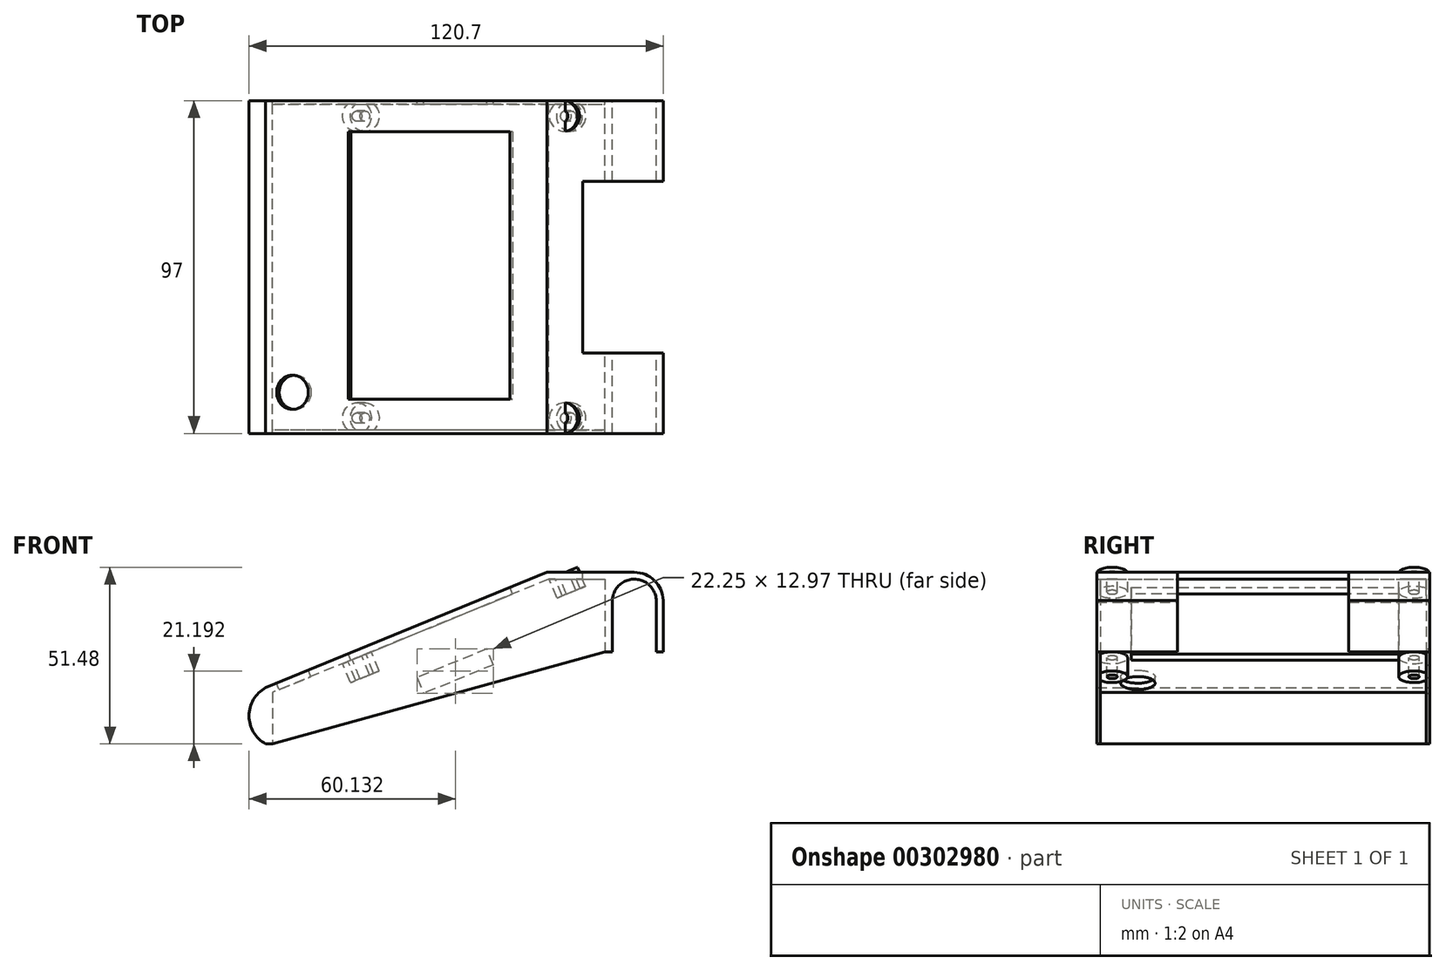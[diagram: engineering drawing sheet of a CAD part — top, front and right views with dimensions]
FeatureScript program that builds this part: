
annotation { "Feature Type Name" : "Feature", "Feature Type Description" : "" }
export const myFeature = defineFeature(function(context is Context, id is Id, definition is map)
    precondition{}
    {
        {
            var Q0;
            Q0=qCreatedBy(makeId("Front.planeOp"),FACE);
            var sketch = newSketch(context, id + "F0", { "sketchPlane" : qUnion([Q0])});
            skLineSegment(sketch, "E0", {"start": v(0, 0) * mm, "end": v(0, 33) * mm, "construction": true});
            skLineSegment(sketch, "E1", {"start": v(0, 33) * mm, "end": v(-80.5, 0) * mm});
            skLineSegment(sketch, "E2", {"start": v(-80.5, 0) * mm, "end": v(-80.5, -15) * mm});
            skLineSegment(sketch, "E3", {"start": v(-80.5, 0) * mm, "end": v(-74.8, -13.88) * mm, "construction": true});
            skLineSegment(sketch, "E4", {"start": v(0, 33) * mm, "end": v(16.42, 33) * mm});
            skLineSegment(sketch, "E5", {"start": v(25, 33) * mm, "end": v(25, 26.6) * mm, "construction": true});
            skArc(sketch, "E6", {"start": v(31.4, 26.3) * mm, "mid": v(25.07, 33) * mm, "end": v(18.6, 26.46) * mm});
            skLineSegment(sketch, "E7.0", {"start": v(-0.4, 35) * mm, "end": v(25.1, 35) * mm});
            skLineSegment(sketch, "E7.1", {"start": v(-0.4, 35) * mm, "end": v(-82.5, 1.34) * mm});
            skLineSegment(sketch, "E7.2", {"start": v(-82.5, 1.34) * mm, "end": v(-82.5, -15) * mm});
            skArc(sketch, "E8.0", {"start": v(33.4, 26.37) * mm, "mid": v(31.02, 32.46) * mm, "end": v(25, 35) * mm});
            skLineSegment(sketch, "E9", {"start": v(0, 33) * mm, "end": v(5.69, 19.12) * mm, "construction": true});
            skLineSegment(sketch, "E10", {"start": v(-82.5, -15) * mm, "end": v(-80.5, -15) * mm});
            skLineSegment(sketch, "E11", {"start": v(33.4, 26.83) * mm, "end": v(33.4, 11.83) * mm});
            skLineSegment(sketch, "E12", {"start": v(31.4, 26.9) * mm, "end": v(31.4, 11.83) * mm});
            skLineSegment(sketch, "E13", {"start": v(31.4, 11.83) * mm, "end": v(33.4, 11.83) * mm});
            skLineSegment(sketch, "E14", {"start": v(16.6, 26.37) * mm, "end": v(16.42, 33) * mm, "construction": true});
            skLineSegment(sketch, "E15", {"start": v(16.42, 33) * mm, "end": v(16.42, 11.83) * mm});
            skLineSegment(sketch, "E16", {"start": v(18.6, 26.46) * mm, "end": v(18.6, 11.83) * mm});
            skLineSegment(sketch, "E17", {"start": v(16.42, 11.83) * mm, "end": v(18.6, 11.83) * mm});
            skSolve(sketch);
        }
        {
            var Q0;
            Q0=makeQuery(id+"F0.imprint","IMPRINT",FACE,{"disambiguationData":[TD([[makeQuery(id+"F0.imprint","IMPRINT",EDGE,{"derivedFrom":sQuery(id+"F0.wireOp",EDGE,"E1")}),-1.0]])]});
            extrude(context, id + "F1", {"entities" : qUnion([Q0]), "endBound" : BoundingType.SYMMETRIC, "depth" : 97 * mm, "offsetDistance" : 25 * mm});
        }
        {
            var Q0;
            Q0=makeQuery(id+"F1.opExtrude","SWEPT_FACE",FACE,{"disambiguationData":[OSD([sQuery(id+"F0.wireOp",EDGE,"E1")])]});
            var sketch = newSketch(context, id + "F2", { "sketchPlane" : qUnion([Q0])});
            skLineSegment(sketch, "E18", {"start": v(17.18, 48.5) * mm, "end": v(17.18, 44) * mm, "construction": true});
            skCircle(sketch, "E19", {"center": v(17.18, 44) * mm, "radius": 1.5 * mm});
            skCircle(sketch, "E20", {"center": v(17.18, 44) * mm, "radius": 4.5 * mm});
            skLineSegment(sketch, "E21", {"start": v(17.18, 44) * mm, "end": v(-47.82, 44) * mm, "construction": true});
            skCircle(sketch, "E22", {"center": v(-47.82, 44) * mm, "radius": 1.5 * mm});
            skCircle(sketch, "E23", {"center": v(-47.82, 44) * mm, "radius": 4.5 * mm});
            skLineSegment(sketch, "E24", {"start": v(17.18, 44) * mm, "end": v(17.18, -44) * mm, "construction": true});
            skCircle(sketch, "E25", {"center": v(17.18, -44) * mm, "radius": 1.5 * mm});
            skCircle(sketch, "E26", {"center": v(17.18, -44) * mm, "radius": 4.5 * mm});
            skLineSegment(sketch, "E27", {"start": v(17.18, -44) * mm, "end": v(-47.82, -44) * mm, "construction": true});
            skCircle(sketch, "E28", {"center": v(-47.82, -44) * mm, "radius": 1.5 * mm});
            skCircle(sketch, "E29", {"center": v(-47.82, -44) * mm, "radius": 4.5 * mm});
            skSolve(sketch);
        }
        {
            var Q0;
            Q0=makeQuery(id+"F2.imprint","IMPRINT",FACE,{"disambiguationData":[TD([[makeQuery(id+"F2.imprint","IMPRINT",EDGE,{"derivedFrom":sQuery(id+"F2.wireOp",EDGE,"E19")}),-1.0]])]});
            var Q1;
            Q1=makeQuery(id+"F2.imprint","IMPRINT",FACE,{"disambiguationData":[TD([[makeQuery(id+"F2.imprint","IMPRINT",EDGE,{"derivedFrom":sQuery(id+"F2.wireOp",EDGE,"E28")}),-1.0]])]});
            var Q2;
            Q2=makeQuery(id+"F2.imprint","IMPRINT",FACE,{"disambiguationData":[TD([[makeQuery(id+"F2.imprint","IMPRINT",EDGE,{"derivedFrom":sQuery(id+"F2.wireOp",EDGE,"E22")}),-1.0]])]});
            var Q3;
            Q3=makeQuery(id+"F2.imprint","IMPRINT",FACE,{"disambiguationData":[TD([[makeQuery(id+"F2.imprint","IMPRINT",EDGE,{"derivedFrom":sQuery(id+"F2.wireOp",EDGE,"E25")}),-1.0]])]});
            extrude(context, id + "F3", {"entities" : qUnion([Q0, Q1, Q2, Q3]), "operationType" : NewBodyOperationType.ADD, "depth" : 6 * mm, "offsetDistance" : 25 * mm});
        }
        {
            var Q0;
            Q0=makeQuery(id+"F1.opExtrude","SWEPT_FACE",FACE,{"disambiguationData":[OSD([sQuery(id+"F0.wireOp",EDGE,"E7.1")])]});
            var sketch = newSketch(context, id + "F4", { "sketchPlane" : qUnion([Q0])});
            skLineSegment(sketch, "E30", {"start": v(1.21, -48.5) * mm, "end": v(1.21, -38.5) * mm, "construction": true});
            skLineSegment(sketch, "E31.bottom", {"start": v(1.21, -38.5) * mm, "end": v(-49.79, -38.5) * mm});
            skLineSegment(sketch, "E31.top", {"start": v(1.21, 39.5) * mm, "end": v(-49.79, 39.5) * mm});
            skLineSegment(sketch, "E31.left", {"start": v(1.21, -38.5) * mm, "end": v(1.21, 39.5) * mm});
            skLineSegment(sketch, "E31.right", {"start": v(-49.79, -38.5) * mm, "end": v(-49.79, 39.5) * mm});
            skLineSegment(sketch, "E32", {"start": v(-67.32, -48.5) * mm, "end": v(-67.32, -36.5) * mm, "construction": true});
            skCircle(sketch, "E33", {"center": v(-67.32, -36.5) * mm, "radius": 5 * mm});
            skSolve(sketch);
        }
        {
            var Q0;
            Q0=makeQuery(id+"F4.imprint","IMPRINT",FACE,{"disambiguationData":[TD([[makeQuery(id+"F4.imprint","IMPRINT",EDGE,{"derivedFrom":sQuery(id+"F4.wireOp",EDGE,"E31.bottom")}),-1.0]])]});
            var Q1;
            Q1=makeQuery(id+"F4.imprint","IMPRINT",FACE,{"disambiguationData":[TD([[makeQuery(id+"F4.imprint","IMPRINT",EDGE,{"derivedFrom":sQuery(id+"F4.wireOp",EDGE,"E33")}),1.0]])]});
            extrude(context, id + "F5", {"entities" : qUnion([Q0, Q1]), "operationType" : NewBodyOperationType.REMOVE, "oppositeDirection" : true, "depth" : 5 * mm, "offsetDistance" : 25 * mm});
        }
        {
            var Q0;
            Q0=makeQuery(id+"F1.opExtrude","CAP_FACE",FACE,{"disambiguationData":[OSD([sQuery(id+"F0.wireOp",EDGE,"E1"),sQuery(id+"F0.wireOp",EDGE,"E2"),sQuery(id+"F0.wireOp",EDGE,"E4"),sQuery(id+"F0.wireOp",EDGE,"E6"),sQuery(id+"F0.wireOp",EDGE,"E7.0"),sQuery(id+"F0.wireOp",EDGE,"E7.1"),sQuery(id+"F0.wireOp",EDGE,"E7.2"),sQuery(id+"F0.wireOp",EDGE,"E8.0"),sQuery(id+"F0.wireOp",EDGE,"E10"),sQuery(id+"F0.wireOp",EDGE,"E11"),sQuery(id+"F0.wireOp",EDGE,"E12"),sQuery(id+"F0.wireOp",EDGE,"E13"),sQuery(id+"F0.wireOp",EDGE,"E15"),sQuery(id+"F0.wireOp",EDGE,"E16"),sQuery(id+"F0.wireOp",EDGE,"E17")])],"isStart":false});
            var sketch = newSketch(context, id + "F6", { "sketchPlane" : qUnion([Q0])});
            skLineSegment(sketch, "E34", {"start": v(16.42, 11.83) * mm, "end": v(-80.5, -15) * mm});
            skSolve(sketch);
        }
        {
            var Q0;
            Q0=makeQuery(id+"F6.imprint","IMPRINT",FACE,{"disambiguationData":[TD([[makeQuery(id+"F6.imprint","IMPRINT",EDGE,{"derivedFrom":sQuery(id+"F6.wireOp",EDGE,"E34")}),-1.0]])]});
            extrude(context, id + "F7", {"entities" : qUnion([Q0]), "operationType" : NewBodyOperationType.ADD, "oppositeDirection" : true, "depth" : 1 * mm, "offsetDistance" : 25 * mm});
        }
        {
            var Q0;
            Q0=makeQuery(id+"F1.opExtrude","CAP_FACE",FACE,{"disambiguationData":[OSD([sQuery(id+"F0.wireOp",EDGE,"E1"),sQuery(id+"F0.wireOp",EDGE,"E2"),sQuery(id+"F0.wireOp",EDGE,"E4"),sQuery(id+"F0.wireOp",EDGE,"E6"),sQuery(id+"F0.wireOp",EDGE,"E7.0"),sQuery(id+"F0.wireOp",EDGE,"E7.1"),sQuery(id+"F0.wireOp",EDGE,"E7.2"),sQuery(id+"F0.wireOp",EDGE,"E8.0"),sQuery(id+"F0.wireOp",EDGE,"E10"),sQuery(id+"F0.wireOp",EDGE,"E11"),sQuery(id+"F0.wireOp",EDGE,"E12"),sQuery(id+"F0.wireOp",EDGE,"E13"),sQuery(id+"F0.wireOp",EDGE,"E15"),sQuery(id+"F0.wireOp",EDGE,"E16"),sQuery(id+"F0.wireOp",EDGE,"E17")])],"isStart":true});
            var sketch = newSketch(context, id + "F8", { "sketchPlane" : qUnion([Q0])});
            skLineSegment(sketch, "E35", {"start": v(80.5, -15) * mm, "end": v(-16.42, 11.83) * mm});
            skSolve(sketch);
        }
        {
            var Q0;
            Q0=makeQuery(id+"F8.imprint","IMPRINT",FACE,{"disambiguationData":[TD([[makeQuery(id+"F8.imprint","IMPRINT",EDGE,{"derivedFrom":sQuery(id+"F8.wireOp",EDGE,"E35")}),-1.0]])]});
            extrude(context, id + "F9", {"entities" : qUnion([Q0]), "operationType" : NewBodyOperationType.ADD, "oppositeDirection" : true, "depth" : 1 * mm, "offsetDistance" : 25 * mm});
        }
        {
            var Q0;
            {var subQ0=sQuery(id+"F0.wireOp",EDGE,"E15");var subQ1=sQuery(id+"F0.wireOp",EDGE,"E4");var subQ2=sQuery(id+"F0.wireOp",EDGE,"E2");var subQ3=sQuery(id+"F0.wireOp",EDGE,"E1");Q0=makeQuery(id+"F9.boolean.opBoolean","MERGE",FACE,{"derivedFrom":[makeQuery(id+"F1.opExtrude","CAP_FACE",FACE,{"disambiguationData":[OSD([subQ3,subQ2,subQ1,sQuery(id+"F0.wireOp",EDGE,"E6"),sQuery(id+"F0.wireOp",EDGE,"E7.0"),sQuery(id+"F0.wireOp",EDGE,"E7.1"),sQuery(id+"F0.wireOp",EDGE,"E7.2"),sQuery(id+"F0.wireOp",EDGE,"E8.0"),sQuery(id+"F0.wireOp",EDGE,"E10"),sQuery(id+"F0.wireOp",EDGE,"E11"),sQuery(id+"F0.wireOp",EDGE,"E12"),sQuery(id+"F0.wireOp",EDGE,"E13"),subQ0,sQuery(id+"F0.wireOp",EDGE,"E16"),sQuery(id+"F0.wireOp",EDGE,"E17")])],"isStart":true}),makeQuery(id+"F9.opExtrude","CAP_FACE",FACE,{"disambiguationData":[OSD([subQ3,subQ2,subQ1,subQ0,sQuery(id+"F8.wireOp",EDGE,"E35")])],"isStart":true})]});}
            var sketch = newSketch(context, id + "F10", { "sketchPlane" : qUnion([Q0])});
            skArc(sketch, "E36", {"start": v(82.5, -15) * mm, "mid": v(87.3, -6.83) * mm, "end": v(82.5, 1.34) * mm});
            skArc(sketch, "E37.0", {"start": v(82.01, -14.13) * mm, "mid": v(86.3, -6.83) * mm, "end": v(82.01, 0.47) * mm});
            skLineSegment(sketch, "E38", {"start": v(82.01, 0.47) * mm, "end": v(82.5, 1.34) * mm});
            skLineSegment(sketch, "E39", {"start": v(82.01, -14.13) * mm, "end": v(82.5, -15) * mm});
            skSolve(sketch);
        }
        {
            var Q0;
            {var subQ0=sQuery(id+"F10.wireOp",EDGE,"E36");Q0=makeQuery(id+"F10.imprint","IMPRINT",FACE,{"disambiguationData":[TD([[makeQuery(id+"F10.imprint","IMPRINT",EDGE,{"derivedFrom":subQ0}),1.0]])]});}
            extrude(context, id + "F11", {"entities" : qUnion([Q0]), "operationType" : NewBodyOperationType.ADD, "oppositeDirection" : true, "depth" : 97 * mm, "offsetDistance" : 25 * mm});
        }
        {
            var Q0;
            {var subQ0=sQuery(id+"F10.wireOp",EDGE,"E37.0");var subQ1=makeQuery(id+"F1.opExtrude","CAP_EDGE",EDGE,{"disambiguationData":[OSD([sQuery(id+"F0.wireOp",EDGE,"E7.2")])],"isStart":true});var subQ2=makeQuery(id+"F10.imprint","INTERSECT",VERTEX,{"disambiguationData":[OD(0.0)],"derivedFrom":[subQ1,subQ0]});Q0=makeQuery(id+"F10.imprint","IMPRINT",FACE,{"disambiguationData":[TD([[makeQuery(id+"F10.imprint","IMPRINT",EDGE,{"disambiguationData":[TD([[subQ2,-1.0]])],"derivedFrom":subQ0}),1.0]])]});}
            extrude(context, id + "F12", {"entities" : qUnion([Q0]), "operationType" : NewBodyOperationType.ADD, "oppositeDirection" : true, "depth" : 97 * mm, "offsetDistance" : 25 * mm});
        }
        {
            var Q0;
            Q0=makeQuery(id+"F1.opExtrude","SWEPT_FACE",FACE,{"disambiguationData":[OSD([sQuery(id+"F0.wireOp",EDGE,"E7.0")])]});
            var sketch = newSketch(context, id + "F13", { "sketchPlane" : qUnion([Q0])});
            skLineSegment(sketch, "E40.bottom", {"start": v(10, -25) * mm, "end": v(40, -25) * mm});
            skLineSegment(sketch, "E40.top", {"start": v(10, 25) * mm, "end": v(40, 25) * mm});
            skLineSegment(sketch, "E40.left", {"start": v(10, -25) * mm, "end": v(10, 25) * mm});
            skLineSegment(sketch, "E40.right", {"start": v(40, -25) * mm, "end": v(40, 25) * mm});
            skPoint(sketch, "E40.middle", {"position": v(25, 0) * mm});
            skSolve(sketch);
        }
        {
            var Q0;
            {var subQ0=sQuery(id+"F13.wireOp",EDGE,"E40.left");Q0=makeQuery(id+"F13.imprint","IMPRINT",FACE,{"disambiguationData":[TD([[makeQuery(id+"F13.imprint","IMPRINT",EDGE,{"derivedFrom":subQ0}),-1.0]])]});}
            var Q1;
            {var subQ0=sQuery(id+"F13.wireOp",EDGE,"E40.right");Q1=makeQuery(id+"F13.imprint","IMPRINT",FACE,{"disambiguationData":[TD([[makeQuery(id+"F13.imprint","IMPRINT",EDGE,{"derivedFrom":subQ0}),1.0]])]});}
            extrude(context, id + "F14", {"entities" : qUnion([Q0, Q1]), "operationType" : NewBodyOperationType.REMOVE, "oppositeDirection" : true, "depth" : 30 * mm, "offsetDistance" : 25 * mm});
        }
        {
            var Q0;
            {var subQ4=sQuery(id+"F10.wireOp",EDGE,"E38");Q0=makeQuery(id+"F10.imprint","IMPRINT",FACE,{"disambiguationData":[TD([[makeQuery(id+"F10.imprint","IMPRINT",EDGE,{"derivedFrom":subQ4}),1.0]])]});}
            var sketch = newSketch(context, id + "F15", { "sketchPlane" : qUnion([Q0])});
            skLineSegment(sketch, "E41.bottom", {"start": v(17.94, 12.68) * mm, "end": v(38.3, 4.33) * mm});
            skLineSegment(sketch, "E42", {"start": v(17.94, 12.68) * mm, "end": v(23.25, 25.63) * mm, "construction": true});
            skLineSegment(sketch, "E43.0", {"start": v(16.04, 8.05) * mm, "end": v(36.4, -0.3) * mm});
            skLineSegment(sketch, "E44", {"start": v(16.04, 8.05) * mm, "end": v(17.94, 12.68) * mm});
            skLineSegment(sketch, "E45", {"start": v(38.3, 4.33) * mm, "end": v(36.4, -0.3) * mm});
            skSolve(sketch);
        }
        {
            var Q0;
            Q0=makeQuery(id+"F15.imprint","IMPRINT",FACE,{"disambiguationData":[TD([[makeQuery(id+"F15.imprint","IMPRINT",EDGE,{"derivedFrom":sQuery(id+"F15.wireOp",EDGE,"E41.bottom")}),-1.0]])]});
            extrude(context, id + "F16", {"entities" : qUnion([Q0]), "operationType" : NewBodyOperationType.REMOVE, "oppositeDirection" : true, "depth" : 2 * mm, "offsetDistance" : 25 * mm});
        }
    });
